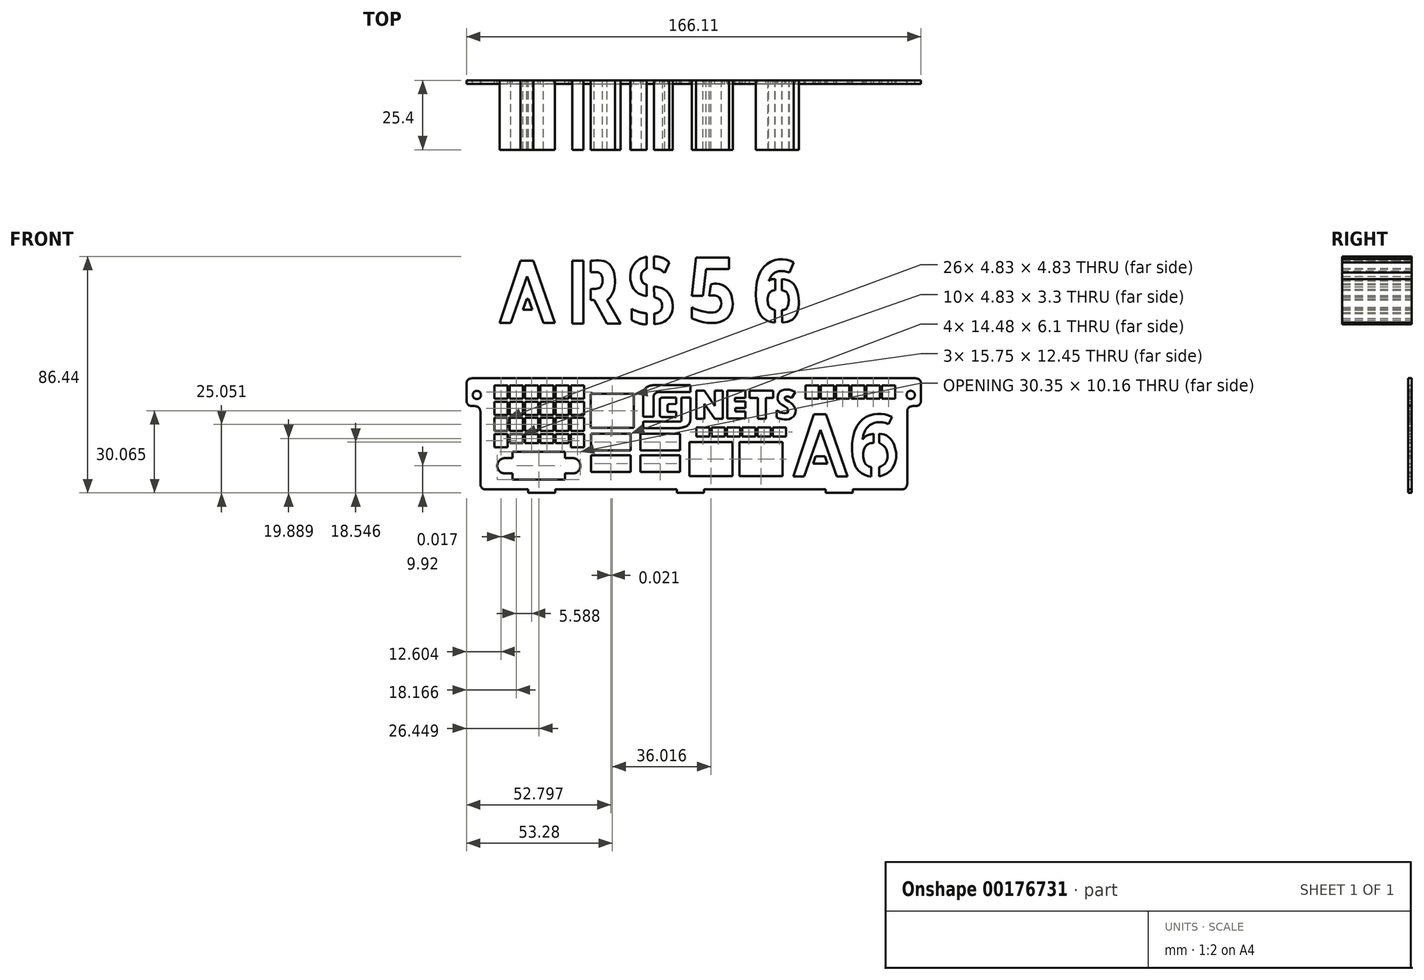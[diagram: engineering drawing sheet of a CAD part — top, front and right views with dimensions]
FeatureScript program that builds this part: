
annotation { "Feature Type Name" : "Feature", "Feature Type Description" : "" }
export const myFeature = defineFeature(function(context is Context, id is Id, definition is map)
    precondition{}
    {
        {
            var Q0;
            Q0=qCreatedBy(makeId("Front.planeOp"),FACE);
            var sketch = newSketch(context, id + "F0", { "sketchPlane" : qUnion([Q0])});
            skLineSegment(sketch, "E0.bottom", {"start": v(-78.63, -3.59) * mm, "end": v(77.32, -3.59) * mm});
            skLineSegment(sketch, "E0.top", {"start": v(-76.63, -44.23) * mm, "end": v(-61.14, -44.23) * mm});
            skLineSegment(sketch, "E0.left", {"start": v(-78.63, -15.75) * mm, "end": v(-78.63, -42.23) * mm});
            skLineSegment(sketch, "E0.right", {"start": v(77.32, -15.75) * mm, "end": v(77.32, -42.23) * mm});
            skLineSegment(sketch, "E1.bottom", {"start": v(-78.63, -3.59) * mm, "end": v(-81.71, -3.59) * mm});
            skLineSegment(sketch, "E1.top", {"start": v(-80.63, -13.75) * mm, "end": v(-81.71, -13.75) * mm});
            skLineSegment(sketch, "E1.right", {"start": v(-83.71, -5.59) * mm, "end": v(-83.71, -11.75) * mm});
            skLineSegment(sketch, "E2.bottom", {"start": v(77.32, -3.59) * mm, "end": v(80.4, -3.59) * mm});
            skLineSegment(sketch, "E2.top", {"start": v(79.32, -13.75) * mm, "end": v(80.4, -13.75) * mm});
            skLineSegment(sketch, "E2.right", {"start": v(82.4, -5.59) * mm, "end": v(82.4, -11.75) * mm});
            skArc(sketch, "E3.filletArc", {"start": v(-81.71, -3.59) * mm, "mid": v(-83.13, -4.17) * mm, "end": v(-83.71, -5.59) * mm});
            skArc(sketch, "E4.filletArc", {"start": v(-83.71, -11.75) * mm, "mid": v(-83.13, -13.16) * mm, "end": v(-81.71, -13.75) * mm});
            skArc(sketch, "E5.filletArc", {"start": v(82.4, -5.59) * mm, "mid": v(81.82, -4.17) * mm, "end": v(80.4, -3.59) * mm});
            skArc(sketch, "E6.filletArc", {"start": v(80.4, -13.75) * mm, "mid": v(81.82, -13.16) * mm, "end": v(82.4, -11.75) * mm});
            skArc(sketch, "E7.filletArc", {"start": v(79.32, -13.75) * mm, "mid": v(77.9, -14.33) * mm, "end": v(77.32, -15.75) * mm});
            skArc(sketch, "E8.filletArc", {"start": v(-78.63, -15.75) * mm, "mid": v(-79.22, -14.33) * mm, "end": v(-80.63, -13.75) * mm});
            skArc(sketch, "E9.filletArc", {"start": v(-78.63, -42.23) * mm, "mid": v(-78.05, -43.64) * mm, "end": v(-76.63, -44.23) * mm});
            skArc(sketch, "E10.filletArc", {"start": v(75.32, -44.23) * mm, "mid": v(76.74, -43.64) * mm, "end": v(77.32, -42.23) * mm});
            skLineSegment(sketch, "E11.top", {"start": v(-61.14, -45.5) * mm, "end": v(-51.23, -45.5) * mm});
            skLineSegment(sketch, "E11.left", {"start": v(-61.14, -44.23) * mm, "end": v(-61.14, -45.5) * mm});
            skLineSegment(sketch, "E11.right", {"start": v(-51.23, -44.23) * mm, "end": v(-51.23, -45.5) * mm});
            skLineSegment(sketch, "E12", {"start": v(-78.55, -42.8) * mm, "end": v(-78.63, -38.65) * mm});
            skLineSegment(sketch, "E13.trimOffspring", {"start": v(-51.23, -44.23) * mm, "end": v(-6.78, -44.23) * mm});
            skLineSegment(sketch, "E14.bottom", {"start": v(-6.78, -45.5) * mm, "end": v(3.12, -45.5) * mm});
            skLineSegment(sketch, "E14.left", {"start": v(-6.78, -45.5) * mm, "end": v(-6.78, -44.23) * mm});
            skLineSegment(sketch, "E14.right", {"start": v(3.12, -45.5) * mm, "end": v(3.12, -44.23) * mm});
            skLineSegment(sketch, "E15.bottom", {"start": v(47.57, -45.5) * mm, "end": v(57.48, -45.5) * mm});
            skLineSegment(sketch, "E15.left", {"start": v(47.57, -45.5) * mm, "end": v(47.57, -44.23) * mm});
            skLineSegment(sketch, "E15.right", {"start": v(57.48, -45.5) * mm, "end": v(57.48, -44.23) * mm});
            skLineSegment(sketch, "E16.trimOffspring", {"start": v(3.12, -44.23) * mm, "end": v(47.57, -44.23) * mm});
            skLineSegment(sketch, "E17.trimOffspring", {"start": v(57.48, -44.23) * mm, "end": v(75.32, -44.23) * mm});
            skCircle(sketch, "E18", {"center": v(-79.9, -9.68) * mm, "radius": 1.52 * mm});
            skLineSegment(sketch, "E19", {"start": v(82.4, -7.66) * mm, "end": v(82.44, -7.66) * mm});
            skCircle(sketch, "E20", {"center": v(78.6, -9.67) * mm, "radius": 1.52 * mm});
            skLineSegment(sketch, "E21.bottom", {"start": v(-66.85, -30.5) * mm, "end": v(-47.67, -30.5) * mm});
            skLineSegment(sketch, "E21.top", {"start": v(-66.85, -40.66) * mm, "end": v(-47.67, -40.66) * mm});
            skLineSegment(sketch, "E21.left", {"start": v(-66.85, -30.5) * mm, "end": v(-66.85, -32.79) * mm});
            skLineSegment(sketch, "E21.right", {"start": v(-47.67, -30.5) * mm, "end": v(-47.67, -32.79) * mm});
            skLineSegment(sketch, "E22.bottom", {"start": v(-66.85, -32.79) * mm, "end": v(-69.64, -32.79) * mm});
            skLineSegment(sketch, "E22.top", {"start": v(-66.85, -38.37) * mm, "end": v(-69.64, -38.37) * mm});
            skLineSegment(sketch, "E23.bottom", {"start": v(-47.67, -38.37) * mm, "end": v(-44.88, -38.37) * mm});
            skLineSegment(sketch, "E23.top", {"start": v(-47.67, -32.79) * mm, "end": v(-44.88, -32.79) * mm});
            skArc(sketch, "E24", {"start": v(-69.64, -32.79) * mm, "mid": v(-72.44, -35.58) * mm, "end": v(-69.64, -38.37) * mm});
            skArc(sketch, "E25", {"start": v(-44.88, -32.79) * mm, "mid": v(-42.08, -35.58) * mm, "end": v(-44.88, -38.37) * mm});
            skLineSegment(sketch, "E26.trimOffspring", {"start": v(-66.85, -38.37) * mm, "end": v(-66.85, -40.66) * mm});
            skLineSegment(sketch, "E27.trimOffspring", {"start": v(-47.67, -38.37) * mm, "end": v(-47.67, -40.66) * mm});
            skLineSegment(sketch, "E28.bottom", {"start": v(-38.3, -9.21) * mm, "end": v(-22.56, -9.21) * mm});
            skLineSegment(sketch, "E28.top", {"start": v(-38.3, -21.66) * mm, "end": v(-22.56, -21.66) * mm});
            skLineSegment(sketch, "E28.left", {"start": v(-38.3, -9.21) * mm, "end": v(-38.3, -21.66) * mm});
            skLineSegment(sketch, "E28.right", {"start": v(-22.56, -9.21) * mm, "end": v(-22.56, -21.66) * mm});
            skLineSegment(sketch, "E29.bottom", {"start": v(-38.15, -23.9) * mm, "end": v(-23.67, -23.9) * mm});
            skLineSegment(sketch, "E29.top", {"start": v(-38.15, -30) * mm, "end": v(-23.67, -30) * mm});
            skLineSegment(sketch, "E29.left", {"start": v(-38.15, -23.9) * mm, "end": v(-38.15, -30) * mm});
            skLineSegment(sketch, "E29.right", {"start": v(-23.67, -23.9) * mm, "end": v(-23.67, -30) * mm});
            skLineSegment(sketch, "E30.bottom", {"start": v(-38.13, -31.75) * mm, "end": v(-23.65, -31.75) * mm});
            skLineSegment(sketch, "E30.top", {"start": v(-38.13, -37.85) * mm, "end": v(-23.65, -37.85) * mm});
            skLineSegment(sketch, "E30.left", {"start": v(-38.13, -31.75) * mm, "end": v(-38.13, -37.85) * mm});
            skLineSegment(sketch, "E30.right", {"start": v(-23.65, -31.75) * mm, "end": v(-23.65, -37.85) * mm});
            skLineSegment(sketch, "E31.bottom", {"start": v(-20.12, -23.9) * mm, "end": v(-5.64, -23.9) * mm});
            skLineSegment(sketch, "E31.top", {"start": v(-20.12, -30) * mm, "end": v(-5.64, -30) * mm});
            skLineSegment(sketch, "E31.left", {"start": v(-20.12, -23.9) * mm, "end": v(-20.12, -30) * mm});
            skLineSegment(sketch, "E31.right", {"start": v(-5.64, -23.9) * mm, "end": v(-5.64, -30) * mm});
            skLineSegment(sketch, "E32.bottom", {"start": v(-20.1, -31.75) * mm, "end": v(-5.62, -31.75) * mm});
            skLineSegment(sketch, "E32.top", {"start": v(-20.1, -37.85) * mm, "end": v(-5.62, -37.85) * mm});
            skLineSegment(sketch, "E32.left", {"start": v(-20.1, -31.75) * mm, "end": v(-20.1, -37.85) * mm});
            skLineSegment(sketch, "E32.right", {"start": v(-5.62, -31.75) * mm, "end": v(-5.62, -37.85) * mm});
            skLineSegment(sketch, "E33.bottom", {"start": v(-2.29, -26.86) * mm, "end": v(13.46, -26.86) * mm});
            skLineSegment(sketch, "E33.top", {"start": v(-2.29, -39.3) * mm, "end": v(13.46, -39.3) * mm});
            skLineSegment(sketch, "E33.left", {"start": v(-2.29, -26.86) * mm, "end": v(-2.29, -39.3) * mm});
            skLineSegment(sketch, "E33.right", {"start": v(13.46, -26.86) * mm, "end": v(13.46, -39.3) * mm});
            skLineSegment(sketch, "E34.bottom", {"start": v(16.1, -26.9) * mm, "end": v(31.85, -26.9) * mm});
            skLineSegment(sketch, "E34.top", {"start": v(16.1, -39.35) * mm, "end": v(31.85, -39.35) * mm});
            skLineSegment(sketch, "E34.left", {"start": v(16.1, -26.9) * mm, "end": v(16.1, -39.35) * mm});
            skLineSegment(sketch, "E34.right", {"start": v(31.85, -26.9) * mm, "end": v(31.85, -39.35) * mm});
            skPoint(sketch, "E35.endSnap0", {"position": v(-78.63, -28.99) * mm});
            skLineSegment(sketch, "E36", {"start": v(-19.1, -9.98) * mm, "end": v(-19.1, -17.6) * mm});
            skLineSegment(sketch, "E37", {"start": v(-19.1, -17.6) * mm, "end": v(-15.3, -17.6) * mm});
            skLineSegment(sketch, "E38", {"start": v(-15.3, -17.6) * mm, "end": v(-15.3, -9.98) * mm});
            skLineSegment(sketch, "E39", {"start": v(-7.04, -17.7) * mm, "end": v(-7.04, -15.88) * mm});
            skLineSegment(sketch, "E40", {"start": v(-5.13, -12.96) * mm, "end": v(-5.13, -18.88) * mm});
            skLineSegment(sketch, "E41", {"start": v(-5.63, -19.38) * mm, "end": v(-19.1, -19.38) * mm});
            skLineSegment(sketch, "E42", {"start": v(-19.1, -19.38) * mm, "end": v(-19.1, -21.77) * mm});
            skLineSegment(sketch, "E43", {"start": v(-19.1, -21.77) * mm, "end": v(-5.9, -21.77) * mm});
            skPoint(sketch, "E44.visualSharp", {"position": v(-13.08, -7.71) * mm});
            skPoint(sketch, "E45.visualSharp", {"position": v(-10.84, -12.27) * mm});
            skArc(sketch, "E45.filletArc", {"start": v(-9.63, -13) * mm, "mid": v(-10, -13.1) * mm, "end": v(-10.24, -13.4) * mm});
            skPoint(sketch, "E46.visualSharp", {"position": v(-5, -19.93) * mm});
            skArc(sketch, "E46.filletArc", {"start": v(-5.63, -19.38) * mm, "mid": v(-5.27, -19.24) * mm, "end": v(-5.13, -18.88) * mm});
            skLineSegment(sketch, "E47", {"start": v(-1.92, -10.67) * mm, "end": v(-1.92, -18.9) * mm});
            skFitSpline(sketch, "E48", {"points": [v(-5.9, -21.77) * mm, v(-4.46, -21.5) * mm, v(-2.54, -20.51) * mm, v(-1.92, -18.9) * mm], "startDerivative": vector(4.44, 0.62) * mm, "endDerivative": vector(1.01, 5.32) * mm});
            skPoint(sketch, "E49.start.orphan", {"position": v(-1.92, -7.71) * mm});
            skPoint(sketch, "E50.visualSharp", {"position": v(-13.08, -10.53) * mm});
            skArc(sketch, "E50.filletArc", {"start": v(-12.11, -10.67) * mm, "mid": v(-12.64, -10.79) * mm, "end": v(-13.08, -11.11) * mm});
            skPoint(sketch, "E51.end.orphan", {"position": v(-1.92, -5.47) * mm});
            skLineSegment(sketch, "E52", {"start": v(-11.8, -8.6) * mm, "end": v(-1.92, -8.6) * mm});
            skLineSegment(sketch, "E53", {"start": v(-1.92, -8.6) * mm, "end": v(-1.92, -6.06) * mm});
            skLineSegment(sketch, "E54", {"start": v(-1.92, -6.06) * mm, "end": v(-14.62, -6.06) * mm});
            skFitSpline(sketch, "E55", {"points": [v(-19.1, -9.98) * mm, v(-18.8, -7.78) * mm, v(-17.02, -6.38) * mm, v(-14.62, -6.06) * mm], "startDerivative": vector(-0.4, 8.89) * mm, "endDerivative": vector(7.51, 0.3) * mm});
            skFitSpline(sketch, "E56", {"points": [v(-11.8, -8.6) * mm, v(-14.12, -8.71) * mm, v(-15.18, -9.54) * mm, v(-15.3, -9.98) * mm], "startDerivative": vector(-5.15, -0.25) * mm, "endDerivative": vector(-1.09, -5.05) * mm});
            skLineSegment(sketch, "E57", {"start": v(0.26, -18.33) * mm, "end": v(3.17, -18.33) * mm});
            skLineSegment(sketch, "E58", {"start": v(3.17, -18.33) * mm, "end": v(3.17, -12.88) * mm});
            skLineSegment(sketch, "E59", {"start": v(3.17, -12.88) * mm, "end": v(6.98, -18.33) * mm});
            skLineSegment(sketch, "E60", {"start": v(6.98, -18.33) * mm, "end": v(9.93, -18.33) * mm});
            skLineSegment(sketch, "E61", {"start": v(9.93, -18.33) * mm, "end": v(9.93, -8.16) * mm});
            skLineSegment(sketch, "E62", {"start": v(9.93, -8.16) * mm, "end": v(6.98, -8.16) * mm});
            skLineSegment(sketch, "E63", {"start": v(6.98, -8.16) * mm, "end": v(6.98, -13.7) * mm});
            skLineSegment(sketch, "E64", {"start": v(6.98, -13.7) * mm, "end": v(3.21, -8.16) * mm});
            skLineSegment(sketch, "E65", {"start": v(3.21, -8.16) * mm, "end": v(0.26, -8.16) * mm});
            skLineSegment(sketch, "E66", {"start": v(0.26, -8.16) * mm, "end": v(0.26, -18.33) * mm});
            skLineSegment(sketch, "E67", {"start": v(11.62, -8.08) * mm, "end": v(11.62, -18.26) * mm});
            skLineSegment(sketch, "E68", {"start": v(11.62, -18.26) * mm, "end": v(18.24, -18.26) * mm});
            skLineSegment(sketch, "E69", {"start": v(18.24, -18.26) * mm, "end": v(18.24, -15.73) * mm});
            skLineSegment(sketch, "E70", {"start": v(18.24, -15.73) * mm, "end": v(14.48, -15.73) * mm});
            skLineSegment(sketch, "E71", {"start": v(14.48, -15.73) * mm, "end": v(14.48, -14.45) * mm});
            skLineSegment(sketch, "E72", {"start": v(14.48, -14.45) * mm, "end": v(18.24, -14.45) * mm});
            skLineSegment(sketch, "E73", {"start": v(18.24, -14.45) * mm, "end": v(18.24, -12.1) * mm});
            skLineSegment(sketch, "E74", {"start": v(18.24, -12.1) * mm, "end": v(14.37, -12.1) * mm});
            skLineSegment(sketch, "E75", {"start": v(14.37, -12.1) * mm, "end": v(14.37, -10.81) * mm});
            skLineSegment(sketch, "E76", {"start": v(14.37, -10.81) * mm, "end": v(18.24, -10.81) * mm});
            skLineSegment(sketch, "E77", {"start": v(18.24, -10.81) * mm, "end": v(18.24, -8.08) * mm});
            skLineSegment(sketch, "E78", {"start": v(18.24, -8.08) * mm, "end": v(11.62, -8.08) * mm});
            skLineSegment(sketch, "E79", {"start": v(19.76, -8.09) * mm, "end": v(28.41, -8.09) * mm});
            skLineSegment(sketch, "E80", {"start": v(28.41, -8.09) * mm, "end": v(28.41, -10.8) * mm});
            skLineSegment(sketch, "E81", {"start": v(19.76, -8.09) * mm, "end": v(19.76, -10.8) * mm});
            skLineSegment(sketch, "E82", {"start": v(25.65, -18.34) * mm, "end": v(22.8, -18.34) * mm});
            skLineSegment(sketch, "E83", {"start": v(22.8, -18.34) * mm, "end": v(22.8, -10.8) * mm});
            skLineSegment(sketch, "E84", {"start": v(19.76, -10.8) * mm, "end": v(22.8, -10.8) * mm});
            skLineSegment(sketch, "E85", {"start": v(25.65, -18.34) * mm, "end": v(25.65, -10.8) * mm});
            skLineSegment(sketch, "E86", {"start": v(25.65, -10.8) * mm, "end": v(28.41, -10.8) * mm});
            skLineSegment(sketch, "E87", {"start": v(29.6, -17.9) * mm, "end": v(29.6, -15.37) * mm});
            skLineSegment(sketch, "E88", {"start": v(35.05, -10.75) * mm, "end": v(36.47, -8.65) * mm});
            skFitSpline(sketch, "E89", {"points": [v(36.47, -8.65) * mm, v(33.2, -7.7) * mm, v(31.05, -8.3) * mm, v(30.04, -9.83) * mm, v(30.27, -12) * mm, v(32, -13.48) * mm, v(33.89, -15.06) * mm, v(33.4, -16.23) * mm, v(31.24, -16.13) * mm, v(29.6, -15.37) * mm], "startDerivative": vector(-29.16, 17.5) * mm, "endDerivative": vector(-22.57, 11.26) * mm});
            skFitSpline(sketch, "E90", {"points": [v(35.05, -10.75) * mm, v(32.7, -10.43) * mm, v(32.7, -11.2) * mm, v(34.09, -12.11) * mm, v(35.77, -13.43) * mm, v(36.58, -15.44) * mm, v(35.7, -17.64) * mm, v(33.45, -18.68) * mm, v(31.3, -18.5) * mm, v(29.6, -17.9) * mm], "startDerivative": vector(-29.3, 17.21) * mm, "endDerivative": vector(-22.92, 10.9) * mm});
            skLineSegment(sketch, "E91", {"start": v(35.7, -39.49) * mm, "end": v(39.66, -39.49) * mm});
            skLineSegment(sketch, "E92", {"start": v(39.66, -39.49) * mm, "end": v(45.59, -22.48) * mm});
            skLineSegment(sketch, "E93", {"start": v(45.59, -22.48) * mm, "end": v(51.6, -39.49) * mm});
            skLineSegment(sketch, "E94", {"start": v(51.6, -39.49) * mm, "end": v(55.53, -39.49) * mm});
            skLineSegment(sketch, "E95", {"start": v(55.53, -39.49) * mm, "end": v(47.64, -16.68) * mm});
            skLineSegment(sketch, "E96", {"start": v(47.64, -16.68) * mm, "end": v(43.25, -16.68) * mm});
            skLineSegment(sketch, "E97", {"start": v(43.25, -16.68) * mm, "end": v(35.7, -39.49) * mm});
            skLineSegment(sketch, "E98", {"start": v(43.83, -32.07) * mm, "end": v(42.95, -34.7) * mm});
            skLineSegment(sketch, "E99", {"start": v(42.95, -34.7) * mm, "end": v(48.15, -34.7) * mm});
            skLineSegment(sketch, "E100", {"start": v(48.15, -34.7) * mm, "end": v(47.27, -32.15) * mm});
            skLineSegment(sketch, "E101", {"start": v(47.27, -32.15) * mm, "end": v(43.83, -32.07) * mm});
            skFitSpline(sketch, "E102", {"points": [v(71.74, -17.73) * mm, v(65.57, -16.68) * mm, v(58.85, -21.24) * mm, v(59, -36.68) * mm, v(63.82, -39.49) * mm, v(64.11, -39.49) * mm], "startDerivative": vector(-31.02, 15.28) * mm, "endDerivative": vector(2.76, 0.83) * mm});
            skLineSegment(sketch, "E103", {"start": v(64.11, -39.49) * mm, "end": v(64.11, -36.1) * mm});
            skLineSegment(sketch, "E104", {"start": v(71.74, -17.73) * mm, "end": v(70.56, -20.29) * mm});
            skFitSpline(sketch, "E105", {"points": [v(70.56, -20.29) * mm, v(66.54, -19.63) * mm, v(62.95, -21.31) * mm, v(60.98, -26) * mm], "startDerivative": vector(-12.66, 4.51) * mm, "endDerivative": vector(-2.14, -16.09) * mm});
            skFitSpline(sketch, "E106", {"points": [v(65, -23.88) * mm, v(62.59, -24.53) * mm, v(60.98, -26) * mm], "startDerivative": vector(-4.74, -0.9) * mm, "endDerivative": vector(-4.87, -5.31) * mm});
            skLineSegment(sketch, "E107", {"start": v(65, -23.88) * mm, "end": v(65, -27.17) * mm});
            skFitSpline(sketch, "E108", {"points": [v(65, -27.17) * mm, v(62.66, -27.9) * mm, v(61.27, -31.2) * mm, v(62.22, -35) * mm, v(64.11, -36.1) * mm], "startDerivative": vector(-11.18, -1.3) * mm, "endDerivative": vector(9.68, -3.32) * mm});
            skLineSegment(sketch, "E109", {"start": v(67.05, -23.88) * mm, "end": v(67.05, -27.17) * mm});
            skLineSegment(sketch, "E110", {"start": v(67.05, -36.1) * mm, "end": v(67.05, -39.49) * mm});
            skFitSpline(sketch, "E111", {"points": [v(67.05, -23.88) * mm, v(71.3, -25.78) * mm, v(73.27, -30.9) * mm, v(71.95, -36.46) * mm, v(67.05, -39.49) * mm], "startDerivative": vector(23.65, 0) * mm, "endDerivative": vector(-21.14, -4.68) * mm});
            skFitSpline(sketch, "E112", {"points": [v(67.05, -27.17) * mm, v(69.54, -29.3) * mm, v(69.76, -33.98) * mm, v(67.05, -36.1) * mm], "startDerivative": vector(9.24, -5.03) * mm, "endDerivative": vector(-10.27, -4.8) * mm});
            skLineSegment(sketch, "E113", {"start": v(-13.08, -11.11) * mm, "end": v(-13.08, -16.98) * mm});
            skLineSegment(sketch, "E114", {"start": v(-7.04, -17.7) * mm, "end": v(-12.13, -17.7) * mm});
            skLineSegment(sketch, "E115", {"start": v(-7.04, -15.88) * mm, "end": v(-9.63, -15.88) * mm});
            skLineSegment(sketch, "E116", {"start": v(-10.24, -13.4) * mm, "end": v(-10.24, -15.37) * mm});
            skFitSpline(sketch, "E117", {"points": [v(-10.24, -15.37) * mm, v(-10.1, -15.8) * mm, v(-9.63, -15.88) * mm], "startDerivative": vector(0.14, -1.07) * mm, "endDerivative": vector(1.08, 0.08) * mm});
            skFitSpline(sketch, "E118", {"points": [v(-13.08, -16.98) * mm, v(-12.82, -17.55) * mm, v(-12.13, -17.7) * mm], "startDerivative": vector(0.03, -1.55) * mm, "endDerivative": vector(1.83, 0.07) * mm});
            skLineSegment(sketch, "E119", {"start": v(-73.48, -6.2) * mm, "end": v(-73.48, -11.03) * mm});
            skLineSegment(sketch, "E120", {"start": v(-73.48, -11.03) * mm, "end": v(-68.65, -11.03) * mm});
            skLineSegment(sketch, "E121", {"start": v(-68.65, -11.03) * mm, "end": v(-68.65, -6.2) * mm});
            skLineSegment(sketch, "E122", {"start": v(-68.65, -6.2) * mm, "end": v(-73.48, -6.2) * mm});
            skLineSegment(sketch, "E123.1.0.0", {"start": v(-63.06, -6.2) * mm, "end": v(-67.9, -6.2) * mm});
            skLineSegment(sketch, "E123.1.0.1", {"start": v(-67.9, -6.2) * mm, "end": v(-67.9, -11.03) * mm});
            skLineSegment(sketch, "E123.1.0.2", {"start": v(-67.9, -11.03) * mm, "end": v(-63.06, -11.03) * mm});
            skLineSegment(sketch, "E123.1.0.3", {"start": v(-63.06, -11.03) * mm, "end": v(-63.06, -6.2) * mm});
            skLineSegment(sketch, "E123.2.0.0", {"start": v(-57.47, -6.2) * mm, "end": v(-62.3, -6.2) * mm});
            skLineSegment(sketch, "E123.2.0.1", {"start": v(-62.3, -6.2) * mm, "end": v(-62.3, -11.03) * mm});
            skLineSegment(sketch, "E123.2.0.2", {"start": v(-62.3, -11.03) * mm, "end": v(-57.47, -11.03) * mm});
            skLineSegment(sketch, "E123.2.0.3", {"start": v(-57.47, -11.03) * mm, "end": v(-57.47, -6.2) * mm});
            skLineSegment(sketch, "E123.3.0.0", {"start": v(-51.88, -6.2) * mm, "end": v(-56.71, -6.2) * mm});
            skLineSegment(sketch, "E123.3.0.1", {"start": v(-56.71, -6.2) * mm, "end": v(-56.71, -11.03) * mm});
            skLineSegment(sketch, "E123.3.0.2", {"start": v(-56.71, -11.03) * mm, "end": v(-51.88, -11.03) * mm});
            skLineSegment(sketch, "E123.3.0.3", {"start": v(-51.88, -11.03) * mm, "end": v(-51.88, -6.2) * mm});
            skLineSegment(sketch, "E123.4.0.0", {"start": v(-46.3, -6.2) * mm, "end": v(-51.13, -6.2) * mm});
            skLineSegment(sketch, "E123.4.0.1", {"start": v(-51.13, -6.2) * mm, "end": v(-51.13, -11.03) * mm});
            skLineSegment(sketch, "E123.4.0.2", {"start": v(-51.13, -11.03) * mm, "end": v(-46.3, -11.03) * mm});
            skLineSegment(sketch, "E123.4.0.3", {"start": v(-46.3, -11.03) * mm, "end": v(-46.3, -6.2) * mm});
            skLineSegment(sketch, "E123.5.0.0", {"start": v(-40.7, -6.2) * mm, "end": v(-45.54, -6.2) * mm});
            skLineSegment(sketch, "E123.5.0.1", {"start": v(-45.54, -6.2) * mm, "end": v(-45.54, -11.03) * mm});
            skLineSegment(sketch, "E123.5.0.2", {"start": v(-45.54, -11.03) * mm, "end": v(-40.7, -11.03) * mm});
            skLineSegment(sketch, "E123.5.0.3", {"start": v(-40.7, -11.03) * mm, "end": v(-40.7, -6.2) * mm});
            skLineSegment(sketch, "E123.direction1", {"start": v(-73.48, -11.03) * mm, "end": v(-67.9, -11.03) * mm, "construction": true});
            skLineSegment(sketch, "E124", {"start": v(-73.5, -12.15) * mm, "end": v(-73.5, -16.98) * mm});
            skLineSegment(sketch, "E125", {"start": v(-73.5, -16.98) * mm, "end": v(-68.67, -16.98) * mm});
            skLineSegment(sketch, "E126", {"start": v(-68.67, -16.98) * mm, "end": v(-68.67, -12.15) * mm});
            skLineSegment(sketch, "E127", {"start": v(-68.67, -12.15) * mm, "end": v(-73.5, -12.15) * mm});
            skLineSegment(sketch, "E128.1.0.0", {"start": v(-63.09, -12.15) * mm, "end": v(-67.92, -12.15) * mm});
            skLineSegment(sketch, "E128.1.0.1", {"start": v(-67.92, -12.15) * mm, "end": v(-67.92, -16.98) * mm});
            skLineSegment(sketch, "E128.1.0.2", {"start": v(-67.92, -16.98) * mm, "end": v(-63.09, -16.98) * mm});
            skLineSegment(sketch, "E128.1.0.3", {"start": v(-63.09, -16.98) * mm, "end": v(-63.09, -12.15) * mm});
            skLineSegment(sketch, "E128.2.0.0", {"start": v(-57.5, -12.15) * mm, "end": v(-62.33, -12.15) * mm});
            skLineSegment(sketch, "E128.2.0.1", {"start": v(-62.33, -12.15) * mm, "end": v(-62.33, -16.98) * mm});
            skLineSegment(sketch, "E128.2.0.2", {"start": v(-62.33, -16.98) * mm, "end": v(-57.5, -16.98) * mm});
            skLineSegment(sketch, "E128.2.0.3", {"start": v(-57.5, -16.98) * mm, "end": v(-57.5, -12.15) * mm});
            skLineSegment(sketch, "E128.3.0.0", {"start": v(-51.9, -12.15) * mm, "end": v(-56.74, -12.15) * mm});
            skLineSegment(sketch, "E128.3.0.1", {"start": v(-56.74, -12.15) * mm, "end": v(-56.74, -16.98) * mm});
            skLineSegment(sketch, "E128.3.0.2", {"start": v(-56.74, -16.98) * mm, "end": v(-51.9, -16.98) * mm});
            skLineSegment(sketch, "E128.3.0.3", {"start": v(-51.9, -16.98) * mm, "end": v(-51.9, -12.15) * mm});
            skLineSegment(sketch, "E128.4.0.0", {"start": v(-46.32, -12.15) * mm, "end": v(-51.15, -12.15) * mm});
            skLineSegment(sketch, "E128.4.0.1", {"start": v(-51.15, -12.15) * mm, "end": v(-51.15, -16.98) * mm});
            skLineSegment(sketch, "E128.4.0.2", {"start": v(-51.15, -16.98) * mm, "end": v(-46.32, -16.98) * mm});
            skLineSegment(sketch, "E128.4.0.3", {"start": v(-46.32, -16.98) * mm, "end": v(-46.32, -12.15) * mm});
            skLineSegment(sketch, "E128.5.0.0", {"start": v(-40.73, -12.15) * mm, "end": v(-45.56, -12.15) * mm});
            skLineSegment(sketch, "E128.5.0.1", {"start": v(-45.56, -12.15) * mm, "end": v(-45.56, -16.98) * mm});
            skLineSegment(sketch, "E128.5.0.2", {"start": v(-45.56, -16.98) * mm, "end": v(-40.73, -16.98) * mm});
            skLineSegment(sketch, "E128.5.0.3", {"start": v(-40.73, -16.98) * mm, "end": v(-40.73, -12.15) * mm});
            skLineSegment(sketch, "E128.direction1", {"start": v(-73.5, -16.98) * mm, "end": v(-67.92, -16.98) * mm, "construction": true});
            skLineSegment(sketch, "E129", {"start": v(-73.52, -18.03) * mm, "end": v(-73.52, -22.86) * mm});
            skLineSegment(sketch, "E130", {"start": v(-73.52, -22.86) * mm, "end": v(-68.7, -22.86) * mm});
            skLineSegment(sketch, "E131", {"start": v(-68.7, -22.86) * mm, "end": v(-68.7, -18.03) * mm});
            skLineSegment(sketch, "E132", {"start": v(-68.7, -18.03) * mm, "end": v(-73.52, -18.03) * mm});
            skLineSegment(sketch, "E133.1.0.0", {"start": v(-63.1, -18.03) * mm, "end": v(-67.93, -18.03) * mm});
            skLineSegment(sketch, "E133.1.0.1", {"start": v(-67.93, -18.03) * mm, "end": v(-67.93, -22.86) * mm});
            skLineSegment(sketch, "E133.1.0.2", {"start": v(-67.93, -22.86) * mm, "end": v(-63.1, -22.86) * mm});
            skLineSegment(sketch, "E133.1.0.3", {"start": v(-63.1, -22.86) * mm, "end": v(-63.1, -18.03) * mm});
            skLineSegment(sketch, "E133.2.0.0", {"start": v(-57.52, -18.03) * mm, "end": v(-62.35, -18.03) * mm});
            skLineSegment(sketch, "E133.2.0.1", {"start": v(-62.35, -18.03) * mm, "end": v(-62.35, -22.86) * mm});
            skLineSegment(sketch, "E133.2.0.2", {"start": v(-62.35, -22.86) * mm, "end": v(-57.52, -22.86) * mm});
            skLineSegment(sketch, "E133.2.0.3", {"start": v(-57.52, -22.86) * mm, "end": v(-57.52, -18.03) * mm});
            skLineSegment(sketch, "E133.3.0.0", {"start": v(-51.93, -18.03) * mm, "end": v(-56.76, -18.03) * mm});
            skLineSegment(sketch, "E133.3.0.1", {"start": v(-56.76, -18.03) * mm, "end": v(-56.76, -22.86) * mm});
            skLineSegment(sketch, "E133.3.0.2", {"start": v(-56.76, -22.86) * mm, "end": v(-51.93, -22.86) * mm});
            skLineSegment(sketch, "E133.3.0.3", {"start": v(-51.93, -22.86) * mm, "end": v(-51.93, -18.03) * mm});
            skLineSegment(sketch, "E133.4.0.0", {"start": v(-46.34, -18.03) * mm, "end": v(-51.17, -18.03) * mm});
            skLineSegment(sketch, "E133.4.0.1", {"start": v(-51.17, -18.03) * mm, "end": v(-51.17, -22.86) * mm});
            skLineSegment(sketch, "E133.4.0.2", {"start": v(-51.17, -22.86) * mm, "end": v(-46.34, -22.86) * mm});
            skLineSegment(sketch, "E133.4.0.3", {"start": v(-46.34, -22.86) * mm, "end": v(-46.34, -18.03) * mm});
            skLineSegment(sketch, "E133.5.0.0", {"start": v(-40.75, -18.03) * mm, "end": v(-45.58, -18.03) * mm});
            skLineSegment(sketch, "E133.5.0.1", {"start": v(-45.58, -18.03) * mm, "end": v(-45.58, -22.86) * mm});
            skLineSegment(sketch, "E133.5.0.2", {"start": v(-45.58, -22.86) * mm, "end": v(-40.75, -22.86) * mm});
            skLineSegment(sketch, "E133.5.0.3", {"start": v(-40.75, -22.86) * mm, "end": v(-40.75, -18.03) * mm});
            skLineSegment(sketch, "E133.direction1", {"start": v(-73.52, -22.86) * mm, "end": v(-67.93, -22.86) * mm, "construction": true});
            skLineSegment(sketch, "E134.1.0.0", {"start": v(-63.13, -23.96) * mm, "end": v(-67.96, -23.96) * mm});
            skLineSegment(sketch, "E134.1.0.1", {"start": v(-67.96, -23.96) * mm, "end": v(-67.96, -27.26) * mm});
            skLineSegment(sketch, "E134.1.0.2", {"start": v(-67.96, -27.26) * mm, "end": v(-63.13, -27.26) * mm});
            skLineSegment(sketch, "E134.1.0.3", {"start": v(-63.13, -27.26) * mm, "end": v(-63.13, -23.96) * mm});
            skLineSegment(sketch, "E134.2.0.0", {"start": v(-57.54, -23.96) * mm, "end": v(-62.37, -23.96) * mm});
            skLineSegment(sketch, "E134.2.0.1", {"start": v(-62.37, -23.96) * mm, "end": v(-62.37, -27.26) * mm});
            skLineSegment(sketch, "E134.2.0.2", {"start": v(-62.37, -27.26) * mm, "end": v(-57.54, -27.26) * mm});
            skLineSegment(sketch, "E134.2.0.3", {"start": v(-57.54, -27.26) * mm, "end": v(-57.54, -23.96) * mm});
            skLineSegment(sketch, "E134.3.0.0", {"start": v(-51.95, -23.96) * mm, "end": v(-56.78, -23.96) * mm});
            skLineSegment(sketch, "E134.3.0.1", {"start": v(-56.78, -23.96) * mm, "end": v(-56.78, -27.26) * mm});
            skLineSegment(sketch, "E134.3.0.2", {"start": v(-56.78, -27.26) * mm, "end": v(-51.95, -27.26) * mm});
            skLineSegment(sketch, "E134.3.0.3", {"start": v(-51.95, -27.26) * mm, "end": v(-51.95, -23.96) * mm});
            skLineSegment(sketch, "E134.4.0.0", {"start": v(-46.36, -23.96) * mm, "end": v(-51.2, -23.96) * mm});
            skLineSegment(sketch, "E134.4.0.1", {"start": v(-51.2, -23.96) * mm, "end": v(-51.2, -27.26) * mm});
            skLineSegment(sketch, "E134.4.0.2", {"start": v(-51.2, -27.26) * mm, "end": v(-46.36, -27.26) * mm});
            skLineSegment(sketch, "E134.4.0.3", {"start": v(-46.36, -27.26) * mm, "end": v(-46.36, -23.96) * mm});
            skLineSegment(sketch, "E134.direction1", {"start": v(-73.55, -27.26) * mm, "end": v(-67.96, -27.26) * mm, "construction": true});
            skLineSegment(sketch, "E135", {"start": v(0.3, -21.52) * mm, "end": v(0.3, -24.82) * mm});
            skLineSegment(sketch, "E136", {"start": v(0.3, -24.82) * mm, "end": v(5.13, -24.82) * mm});
            skLineSegment(sketch, "E137", {"start": v(5.13, -24.82) * mm, "end": v(5.13, -21.52) * mm});
            skLineSegment(sketch, "E138", {"start": v(5.13, -21.52) * mm, "end": v(0.3, -21.52) * mm});
            skLineSegment(sketch, "E139.1.0.0", {"start": v(10.72, -21.52) * mm, "end": v(5.89, -21.52) * mm});
            skLineSegment(sketch, "E139.1.0.1", {"start": v(5.89, -21.52) * mm, "end": v(5.89, -24.82) * mm});
            skLineSegment(sketch, "E139.1.0.2", {"start": v(5.89, -24.82) * mm, "end": v(10.72, -24.82) * mm});
            skLineSegment(sketch, "E139.1.0.3", {"start": v(10.72, -24.82) * mm, "end": v(10.72, -21.52) * mm});
            skLineSegment(sketch, "E139.2.0.0", {"start": v(16.3, -21.52) * mm, "end": v(11.47, -21.52) * mm});
            skLineSegment(sketch, "E139.2.0.1", {"start": v(11.47, -21.52) * mm, "end": v(11.47, -24.82) * mm});
            skLineSegment(sketch, "E139.2.0.2", {"start": v(11.47, -24.82) * mm, "end": v(16.3, -24.82) * mm});
            skLineSegment(sketch, "E139.2.0.3", {"start": v(16.3, -24.82) * mm, "end": v(16.3, -21.52) * mm});
            skLineSegment(sketch, "E139.3.0.0", {"start": v(21.9, -21.52) * mm, "end": v(17.06, -21.52) * mm});
            skLineSegment(sketch, "E139.3.0.1", {"start": v(17.06, -21.52) * mm, "end": v(17.06, -24.82) * mm});
            skLineSegment(sketch, "E139.3.0.2", {"start": v(17.06, -24.82) * mm, "end": v(21.9, -24.82) * mm});
            skLineSegment(sketch, "E139.3.0.3", {"start": v(21.9, -24.82) * mm, "end": v(21.9, -21.52) * mm});
            skLineSegment(sketch, "E139.4.0.0", {"start": v(27.48, -21.52) * mm, "end": v(22.65, -21.52) * mm});
            skLineSegment(sketch, "E139.4.0.1", {"start": v(22.65, -21.52) * mm, "end": v(22.65, -24.82) * mm});
            skLineSegment(sketch, "E139.4.0.2", {"start": v(22.65, -24.82) * mm, "end": v(27.48, -24.82) * mm});
            skLineSegment(sketch, "E139.4.0.3", {"start": v(27.48, -24.82) * mm, "end": v(27.48, -21.52) * mm});
            skLineSegment(sketch, "E139.5.0.0", {"start": v(33.07, -21.52) * mm, "end": v(28.24, -21.52) * mm});
            skLineSegment(sketch, "E139.5.0.1", {"start": v(28.24, -21.52) * mm, "end": v(28.24, -24.82) * mm});
            skLineSegment(sketch, "E139.5.0.2", {"start": v(28.24, -24.82) * mm, "end": v(33.07, -24.82) * mm});
            skLineSegment(sketch, "E139.5.0.3", {"start": v(33.07, -24.82) * mm, "end": v(33.07, -21.52) * mm});
            skLineSegment(sketch, "E139.direction1", {"start": v(0.3, -24.82) * mm, "end": v(5.89, -24.82) * mm, "construction": true});
            skLineSegment(sketch, "E140", {"start": v(40.11, -6.22) * mm, "end": v(40.11, -11.05) * mm});
            skLineSegment(sketch, "E141", {"start": v(40.11, -11.05) * mm, "end": v(44.94, -11.05) * mm});
            skLineSegment(sketch, "E142", {"start": v(44.94, -11.05) * mm, "end": v(44.94, -6.22) * mm});
            skLineSegment(sketch, "E143", {"start": v(44.94, -6.22) * mm, "end": v(40.11, -6.22) * mm});
            skLineSegment(sketch, "E144.1.0.0", {"start": v(50.53, -6.22) * mm, "end": v(45.7, -6.22) * mm});
            skLineSegment(sketch, "E144.1.0.1", {"start": v(45.7, -6.22) * mm, "end": v(45.7, -11.05) * mm});
            skLineSegment(sketch, "E144.1.0.2", {"start": v(45.7, -11.05) * mm, "end": v(50.53, -11.05) * mm});
            skLineSegment(sketch, "E144.1.0.3", {"start": v(50.53, -11.05) * mm, "end": v(50.53, -6.22) * mm});
            skLineSegment(sketch, "E144.2.0.0", {"start": v(56.12, -6.22) * mm, "end": v(51.29, -6.22) * mm});
            skLineSegment(sketch, "E144.2.0.1", {"start": v(51.29, -6.22) * mm, "end": v(51.29, -11.05) * mm});
            skLineSegment(sketch, "E144.2.0.2", {"start": v(51.29, -11.05) * mm, "end": v(56.12, -11.05) * mm});
            skLineSegment(sketch, "E144.2.0.3", {"start": v(56.12, -11.05) * mm, "end": v(56.12, -6.22) * mm});
            skLineSegment(sketch, "E144.3.0.0", {"start": v(61.7, -6.22) * mm, "end": v(56.88, -6.22) * mm});
            skLineSegment(sketch, "E144.3.0.1", {"start": v(56.88, -6.22) * mm, "end": v(56.88, -11.05) * mm});
            skLineSegment(sketch, "E144.3.0.2", {"start": v(56.88, -11.05) * mm, "end": v(61.7, -11.05) * mm});
            skLineSegment(sketch, "E144.3.0.3", {"start": v(61.7, -11.05) * mm, "end": v(61.7, -6.22) * mm});
            skLineSegment(sketch, "E144.4.0.0", {"start": v(67.3, -6.22) * mm, "end": v(62.46, -6.22) * mm});
            skLineSegment(sketch, "E144.4.0.1", {"start": v(62.46, -6.22) * mm, "end": v(62.46, -11.05) * mm});
            skLineSegment(sketch, "E144.4.0.2", {"start": v(62.46, -11.05) * mm, "end": v(67.3, -11.05) * mm});
            skLineSegment(sketch, "E144.4.0.3", {"start": v(67.3, -11.05) * mm, "end": v(67.3, -6.22) * mm});
            skLineSegment(sketch, "E144.5.0.0", {"start": v(72.88, -6.22) * mm, "end": v(68.05, -6.22) * mm});
            skLineSegment(sketch, "E144.5.0.1", {"start": v(68.05, -6.22) * mm, "end": v(68.05, -11.05) * mm});
            skLineSegment(sketch, "E144.5.0.2", {"start": v(68.05, -11.05) * mm, "end": v(72.88, -11.05) * mm});
            skLineSegment(sketch, "E144.5.0.3", {"start": v(72.88, -11.05) * mm, "end": v(72.88, -6.22) * mm});
            skLineSegment(sketch, "E144.direction1", {"start": v(40.11, -11.05) * mm, "end": v(45.7, -11.05) * mm, "construction": true});
            skLineSegment(sketch, "E145", {"start": v(-7.04, -12.98) * mm, "end": v(-7.06, -10.67) * mm});
            skLineSegment(sketch, "E146", {"start": v(-5.13, -12.96) * mm, "end": v(-5.13, -10.67) * mm});
            skLineSegment(sketch, "E147", {"start": v(-7.04, -12.98) * mm, "end": v(-9.63, -13) * mm});
            skLineSegment(sketch, "E148", {"start": v(-7.06, -10.67) * mm, "end": v(-12.11, -10.67) * mm});
            skLineSegment(sketch, "E149", {"start": v(-5.13, -10.67) * mm, "end": v(-1.92, -10.67) * mm});
            skLineSegment(sketch, "E150.5.0.0", {"start": v(-68.67, -23.93) * mm, "end": v(-73.5, -23.93) * mm});
            skLineSegment(sketch, "E150.5.0.1", {"start": v(-73.5, -23.93) * mm, "end": v(-73.5, -28.76) * mm});
            skLineSegment(sketch, "E150.5.0.2", {"start": v(-73.5, -28.76) * mm, "end": v(-68.67, -28.76) * mm});
            skLineSegment(sketch, "E150.5.0.3", {"start": v(-68.67, -28.76) * mm, "end": v(-68.67, -23.93) * mm});
            skLineSegment(sketch, "E151.5.0.0", {"start": v(-40.73, -23.92) * mm, "end": v(-45.56, -23.92) * mm});
            skLineSegment(sketch, "E151.5.0.1", {"start": v(-45.56, -23.92) * mm, "end": v(-45.56, -28.75) * mm});
            skLineSegment(sketch, "E151.5.0.2", {"start": v(-45.56, -28.75) * mm, "end": v(-40.73, -28.75) * mm});
            skLineSegment(sketch, "E151.5.0.3", {"start": v(-40.73, -28.75) * mm, "end": v(-40.73, -23.92) * mm});
            skSolve(sketch);
        }
        {
            var Q0;
            {var subQ3=sQuery(id+"F0.wireOp",EDGE,"E12");Q0=makeQuery(id+"F0.imprint","IMPRINT",FACE,{"disambiguationData":[TD([[makeQuery(id+"F0.imprint","IMPRINT",EDGE,{"derivedFrom":subQ3}),1.0]])]});}
            var Q1;
            Q1=makeQuery(id+"F0.imprint","IMPRINT",FACE,{"disambiguationData":[TD([[makeQuery(id+"F0.imprint","IMPRINT",EDGE,{"derivedFrom":sQuery(id+"F0.wireOp",EDGE,"E0.bottom")}),-1.0]])]});
            var Q2;
            Q2=makeQuery(id+"F0.imprint","IMPRINT",FACE,{"disambiguationData":[TD([[makeQuery(id+"F0.imprint","IMPRINT",EDGE,{"derivedFrom":sQuery(id+"F0.wireOp",EDGE,"3ce2acb7-87bb-4b37-b970-fa6a4dae83fd")}),-1.0]])]});
            extrude(context, id + "F1", {"entities" : qUnion([Q0, Q1, Q2]), "depth" : 1.27 * mm});
        }
        {
            var Q0;
            Q0=qCreatedBy(makeId("Front.planeOp"),FACE);
            var sketch = newSketch(context, id + "F2", { "sketchPlane" : qUnion([Q0])});
            skLineSegment(sketch, "E152", {"start": v(-9.66, 38.76) * mm, "end": v(-11.26, 35) * mm});
            skLineSegment(sketch, "E153", {"start": v(-23.32, 17.74) * mm, "end": v(-23.3, 21.82) * mm});
            skLineSegment(sketch, "E154", {"start": v(12.22, 40.55) * mm, "end": v(12.22, 36.36) * mm});
            skLineSegment(sketch, "E155", {"start": v(12.22, 36.36) * mm, "end": v(3.87, 36.36) * mm});
            skLineSegment(sketch, "E156", {"start": v(3.87, 36.36) * mm, "end": v(2.7, 26.62) * mm});
            skLineSegment(sketch, "E157", {"start": v(2.7, 26.62) * mm, "end": v(-1.37, 26.62) * mm});
            skLineSegment(sketch, "E158", {"start": v(-1.37, 26.62) * mm, "end": v(0.22, 40.5) * mm});
            skLineSegment(sketch, "E159", {"start": v(0.22, 40.5) * mm, "end": v(12.22, 40.55) * mm});
            skLineSegment(sketch, "E160", {"start": v(4.99, 26.62) * mm, "end": v(5.66, 30.8) * mm});
            skLineSegment(sketch, "E161", {"start": v(-1.37, 18.36) * mm, "end": v(-1.37, 22.41) * mm});
            skFitSpline(sketch, "E162", {"points": [v(-1.37, 18.36) * mm, v(3.86, 16.8) * mm, v(9.68, 17.27) * mm, v(13.07, 20.59) * mm, v(13.3, 25.9) * mm, v(11.33, 29.58) * mm, v(8.15, 31) * mm, v(5.66, 30.8) * mm], "startDerivative": vector(31.26, -12.34) * mm, "endDerivative": vector(-26.75, -5.12) * mm});
            skFitSpline(sketch, "E163", {"points": [v(4.99, 26.62) * mm, v(7.13, 26.7) * mm, v(8.9, 25.67) * mm, v(9.29, 22.87) * mm, v(8.11, 21.05) * mm, v(5.66, 20.46) * mm, v(-1.37, 22.41) * mm], "startDerivative": vector(20.92, 1.06) * mm, "endDerivative": vector(-24.73, 15.46) * mm});
            skFitSpline(sketch, "E164", {"points": [v(35.92, 38.78) * mm, v(29.73, 39.83) * mm, v(23.24, 34.44) * mm, v(23.26, 20.41) * mm, v(26.26, 17.49) * mm, v(29, 16.83) * mm], "startDerivative": vector(-31.18, 15.35) * mm, "endDerivative": vector(25.5, 0) * mm});
            skLineSegment(sketch, "E165", {"start": v(29, 16.83) * mm, "end": v(29, 21.33) * mm});
            skLineSegment(sketch, "E166", {"start": v(35.92, 38.78) * mm, "end": v(34.32, 35.03) * mm});
            skFitSpline(sketch, "E167", {"points": [v(34.32, 35.03) * mm, v(30.54, 35.56) * mm, v(28.38, 34.61) * mm, v(26.74, 32.01) * mm], "startDerivative": vector(-12.66, 4.51) * mm, "endDerivative": vector(-5.25, -11.82) * mm});
            skFitSpline(sketch, "E168", {"points": [v(29.17, 32.63) * mm, v(27.87, 32.6) * mm, v(26.74, 32.01) * mm], "startDerivative": vector(-4.59, 0.7) * mm, "endDerivative": vector(-4.27, -3.1) * mm});
            skLineSegment(sketch, "E169", {"start": v(29.17, 32.63) * mm, "end": v(29.17, 28.64) * mm});
            skFitSpline(sketch, "E170", {"points": [v(29.17, 28.64) * mm, v(27.02, 27.72) * mm, v(26.37, 24.6) * mm, v(27.09, 22.38) * mm, v(29, 21.33) * mm], "startDerivative": vector(-11.18, -1.3) * mm, "endDerivative": vector(11.76, -5.04) * mm});
            skLineSegment(sketch, "E171", {"start": v(31.59, 32.63) * mm, "end": v(31.59, 28.64) * mm});
            skLineSegment(sketch, "E172", {"start": v(31.59, 21.33) * mm, "end": v(31.65, 16.83) * mm});
            skFitSpline(sketch, "E173", {"points": [v(31.59, 32.63) * mm, v(35.82, 30.85) * mm, v(37.65, 25.83) * mm, v(36.4, 18.91) * mm, v(31.65, 16.83) * mm], "startDerivative": vector(25.33, -0.24) * mm, "endDerivative": vector(-23.4, 1) * mm});
            skFitSpline(sketch, "E174", {"points": [v(31.59, 28.64) * mm, v(33.67, 27.2) * mm, v(33.6, 22.64) * mm, v(31.59, 21.33) * mm], "startDerivative": vector(9.64, -2.08) * mm, "endDerivative": vector(-10.64, -0.7) * mm});
            skLineSegment(sketch, "E175", {"start": v(-71.56, 16.65) * mm, "end": v(-67.47, 16.65) * mm});
            skLineSegment(sketch, "E176", {"start": v(-67.47, 16.65) * mm, "end": v(-61.53, 33.66) * mm});
            skLineSegment(sketch, "E177", {"start": v(-61.53, 33.66) * mm, "end": v(-55.53, 16.65) * mm});
            skLineSegment(sketch, "E178", {"start": v(-55.53, 16.65) * mm, "end": v(-51.37, 16.65) * mm});
            skLineSegment(sketch, "E179", {"start": v(-51.37, 16.65) * mm, "end": v(-59.26, 39.46) * mm});
            skLineSegment(sketch, "E180", {"start": v(-59.26, 39.46) * mm, "end": v(-64.01, 39.46) * mm});
            skLineSegment(sketch, "E181", {"start": v(-64.01, 39.46) * mm, "end": v(-71.56, 16.65) * mm});
            skLineSegment(sketch, "E182", {"start": v(-61.72, 25.43) * mm, "end": v(-63.05, 21.43) * mm});
            skLineSegment(sketch, "E183", {"start": v(-63.05, 21.43) * mm, "end": v(-59.7, 21.43) * mm});
            skLineSegment(sketch, "E184", {"start": v(-59.7, 21.43) * mm, "end": v(-61.08, 25.42) * mm});
            skLineSegment(sketch, "E185", {"start": v(-61.08, 25.42) * mm, "end": v(-61.72, 25.43) * mm});
            skLineSegment(sketch, "E186", {"start": v(-45.07, 16.4) * mm, "end": v(-40.93, 16.4) * mm});
            skLineSegment(sketch, "E187", {"start": v(-45.07, 16.4) * mm, "end": v(-45.07, 39.4) * mm});
            skLineSegment(sketch, "E188", {"start": v(-45.07, 39.4) * mm, "end": v(-40.93, 39.4) * mm});
            skLineSegment(sketch, "E189", {"start": v(-40.93, 39.4) * mm, "end": v(-40.93, 16.4) * mm});
            skLineSegment(sketch, "E190", {"start": v(-38.37, 39.4) * mm, "end": v(-38.37, 35.22) * mm});
            skLineSegment(sketch, "E191", {"start": v(-38.37, 29.03) * mm, "end": v(-38.37, 25) * mm});
            skFitSpline(sketch, "E192", {"points": [v(-38.37, 35.22) * mm, v(-34.49, 34.38) * mm, v(-34.49, 30.04) * mm, v(-38.37, 29.03) * mm], "startDerivative": vector(18.5, 0.8) * mm, "endDerivative": vector(-17.69, -1.47) * mm});
            skFitSpline(sketch, "E193", {"points": [v(-38.37, 39.4) * mm, v(-31.57, 38.24) * mm, v(-29.53, 30.5) * mm, v(-32.4, 25) * mm], "startDerivative": vector(23.64, 1.15) * mm, "endDerivative": vector(-16.34, -10.4) * mm});
            skLineSegment(sketch, "E194", {"start": v(-38.37, 25) * mm, "end": v(-37.1, 25) * mm});
            skLineSegment(sketch, "E195", {"start": v(-37.1, 25) * mm, "end": v(-32.33, 16.4) * mm});
            skLineSegment(sketch, "E196", {"start": v(-32.33, 16.4) * mm, "end": v(-27.36, 16.4) * mm});
            skLineSegment(sketch, "E197", {"start": v(-27.36, 16.4) * mm, "end": v(-32.4, 25) * mm});
            skFitSpline(sketch, "E198", {"points": [v(-9.66, 38.76) * mm, v(-11.92, 40.39) * mm, v(-15.17, 40.9) * mm], "startDerivative": vector(-5.08, 5.12) * mm, "endDerivative": vector(-6.35, -0.67) * mm});
            skFitSpline(sketch, "E199", {"points": [v(-11.26, 35) * mm, v(-13.31, 36.32) * mm, v(-15.16, 36.58) * mm], "startDerivative": vector(-3.94, 2.83) * mm, "endDerivative": vector(-3.9, 0.23) * mm});
            skFitSpline(sketch, "E200", {"points": [v(-23.32, 17.74) * mm, v(-20.28, 16.4) * mm, v(-17.89, 16.16) * mm], "startDerivative": vector(5.73, -3.03) * mm, "endDerivative": vector(5.11, -0.05) * mm});
            skFitSpline(sketch, "E201", {"points": [v(-23.3, 21.82) * mm, v(-20.56, 20.62) * mm, v(-17.89, 20.11) * mm], "startDerivative": vector(5.73, -3.46) * mm, "endDerivative": vector(8.1, -1.24) * mm});
            skFitSpline(sketch, "E202", {"points": [v(-15.11, 16.17) * mm, v(-12.2, 16.8) * mm, v(-9.83, 18.43) * mm, v(-8.28, 22.6) * mm, v(-10.47, 28.13) * mm, v(-15.17, 29.93) * mm], "startDerivative": vector(16.3, 1.36) * mm, "endDerivative": vector(-19.9, 0) * mm});
            skFitSpline(sketch, "E203", {"points": [v(-15.11, 20.05) * mm, v(-12.56, 21.45) * mm, v(-12.74, 24.76) * mm, v(-15.14, 26.06) * mm], "startDerivative": vector(8.12, 0.64) * mm, "endDerivative": vector(-8.75, 2.5) * mm});
            skFitSpline(sketch, "E204", {"points": [v(-17.89, 40.9) * mm, v(-22.22, 38.48) * mm, v(-23.88, 33.92) * mm, v(-22.64, 29.19) * mm, v(-17.89, 26.4) * mm], "startDerivative": vector(-23.24, -7.21) * mm, "endDerivative": vector(29.14, -6.41) * mm});
            skFitSpline(sketch, "E205", {"points": [v(-17.89, 36.44) * mm, v(-19.36, 35.4) * mm, v(-19.95, 33.54) * mm, v(-19.16, 31.33) * mm, v(-17.89, 30.64) * mm], "startDerivative": vector(-8.75, -3.12) * mm, "endDerivative": vector(7.16, -2.61) * mm});
            skLineSegment(sketch, "E206", {"start": v(-17.89, 40.9) * mm, "end": v(-17.89, 36.44) * mm});
            skLineSegment(sketch, "E207", {"start": v(-15.17, 40.9) * mm, "end": v(-15.16, 36.58) * mm});
            skLineSegment(sketch, "E208", {"start": v(-17.89, 30.64) * mm, "end": v(-17.89, 26.4) * mm});
            skLineSegment(sketch, "E209", {"start": v(-15.17, 29.93) * mm, "end": v(-15.14, 26.06) * mm});
            skLineSegment(sketch, "E210", {"start": v(-17.89, 20.11) * mm, "end": v(-17.89, 16.16) * mm});
            skLineSegment(sketch, "E211", {"start": v(-15.11, 20.05) * mm, "end": v(-15.11, 16.17) * mm});
            skSolve(sketch);
        }
        {
            var Q0;
            Q0=makeQuery(id+"F2.imprint","IMPRINT",FACE,{"disambiguationData":[TD([[makeQuery(id+"F2.imprint","IMPRINT",EDGE,{"derivedFrom":sQuery(id+"F2.wireOp",EDGE,"E175")}),1.0]])]});
            var Q1;
            Q1=makeQuery(id+"F2.imprint","IMPRINT",FACE,{"disambiguationData":[TD([[makeQuery(id+"F2.imprint","IMPRINT",EDGE,{"derivedFrom":sQuery(id+"F2.wireOp",EDGE,"E182")}),1.0]])]});
            var Q2;
            Q2=makeQuery(id+"F2.imprint","IMPRINT",FACE,{"disambiguationData":[TD([[makeQuery(id+"F2.imprint","IMPRINT",EDGE,{"derivedFrom":sQuery(id+"F2.wireOp",EDGE,"0d03a92f-a249-4235-a711-afd2db5765d1.sketch_text.stroke-0")}),-1.0]])]});
            var Q3;
            Q3 = qSketchRegion(id + "F2", true);
            extrude(context, id + "F3", {"entities" : qUnion([Q0, Q1, Q2, Q3]), "depth" : 25.4 * mm});
        }
    });
